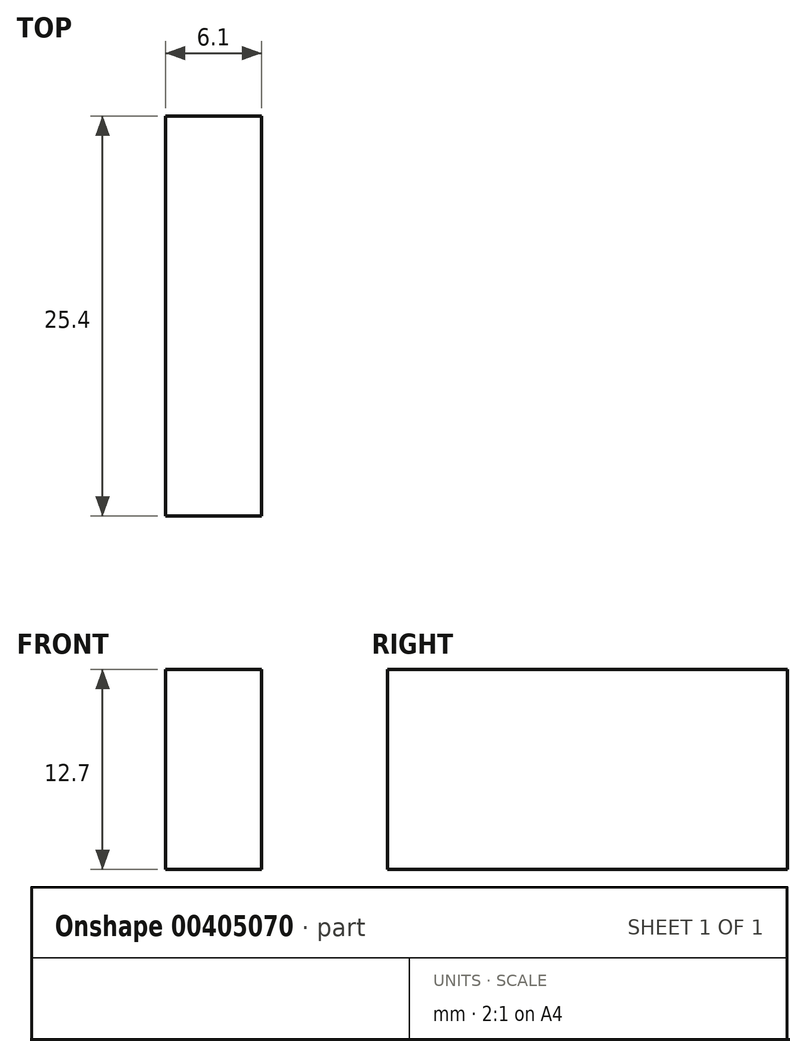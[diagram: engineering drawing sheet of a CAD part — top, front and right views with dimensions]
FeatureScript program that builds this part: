
annotation { "Feature Type Name" : "Feature", "Feature Type Description" : "" }
export const myFeature = defineFeature(function(context is Context, id is Id, definition is map)
    precondition{}
    {
        {
            var Q0;
            Q0=qCreatedBy(makeId("Right.planeOp"),FACE);
            var sketch = newSketch(context, id + "F0", { "sketchPlane" : qUnion([Q0])});
            skLineSegment(sketch, "E0.bottom", {"start": v(-25.4, 27.91) * mm, "end": v(0, 27.91) * mm});
            skLineSegment(sketch, "E0.top", {"start": v(-25.4, 15.21) * mm, "end": v(0, 15.21) * mm});
            skLineSegment(sketch, "E0.left", {"start": v(-25.4, 27.91) * mm, "end": v(-25.4, 15.21) * mm});
            skLineSegment(sketch, "E0.right", {"start": v(0, 27.91) * mm, "end": v(0, 15.21) * mm});
            skSolve(sketch);
        }
        {
            var Q0;
            Q0=makeQuery(id+"F0.imprint","IMPRINT",FACE,{"disambiguationData":[TD([[makeQuery(id+"F0.imprint","IMPRINT",EDGE,{"derivedFrom":sQuery(id+"F0.wireOp",EDGE,"E0.bottom")}),-1.0]])]});
            extrude(context, id + "F1", {"entities" : qUnion([Q0]), "depth" : 6.1 * mm});
        }
    });
